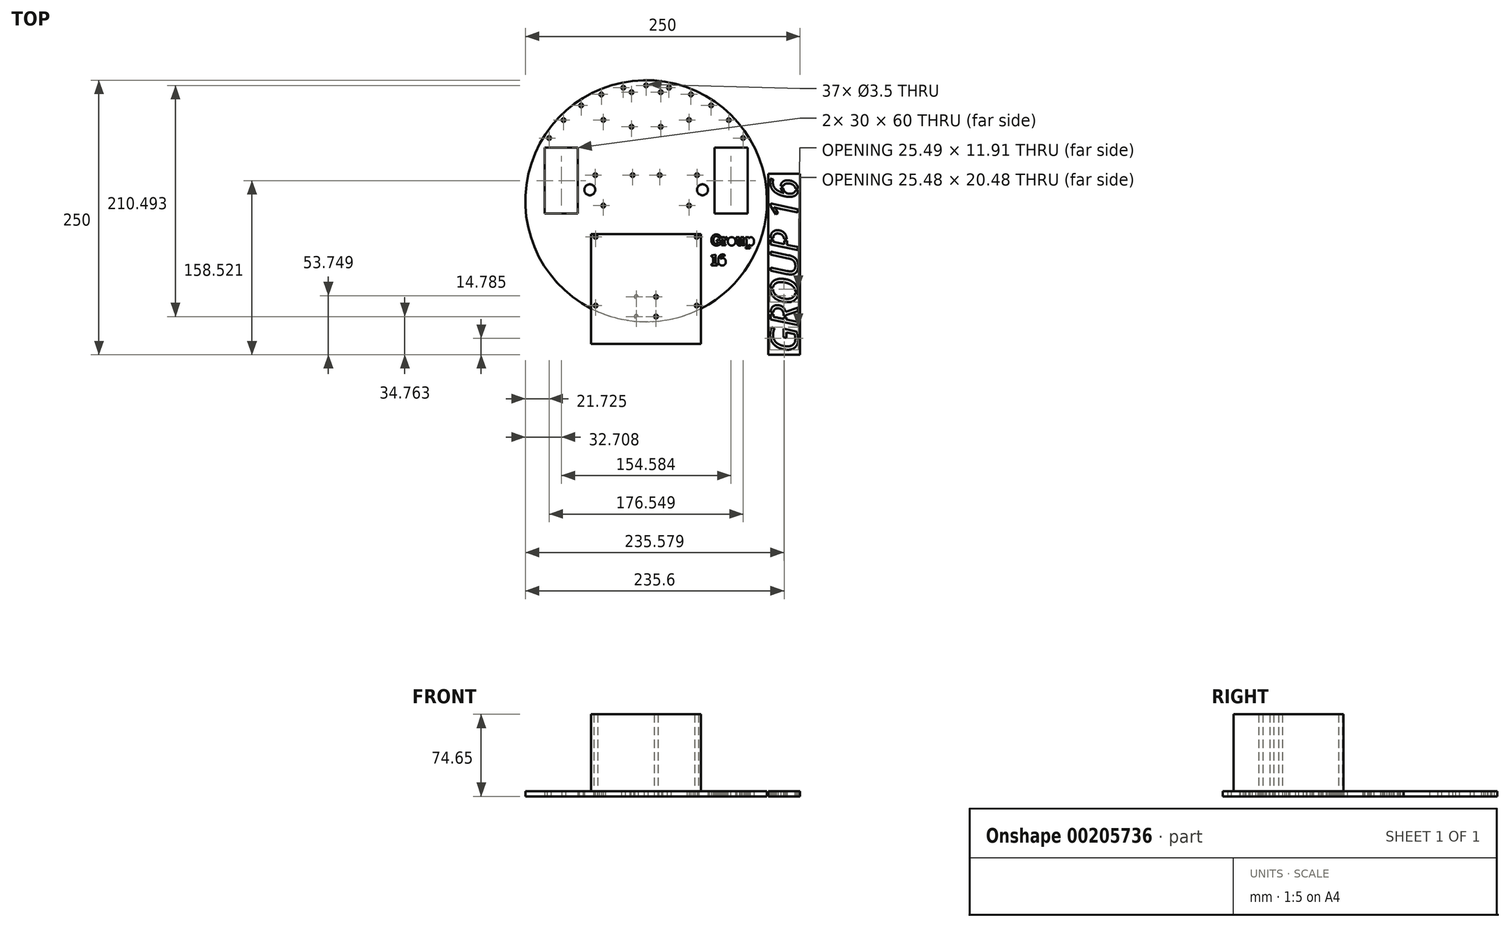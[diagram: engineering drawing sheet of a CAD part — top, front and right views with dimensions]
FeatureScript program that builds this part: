
annotation { "Feature Type Name" : "Feature", "Feature Type Description" : "" }
export const myFeature = defineFeature(function(context is Context, id is Id, definition is map)
    precondition{}
    {
        {
            var Q0;
            Q0=qCreatedBy(makeId("Top.planeOp"),FACE);
            var sketch = newSketch(context, id + "F0", { "sketchPlane" : qUnion([Q0])});
            skCircle(sketch, "E0", {"center": v(0, 0) * mm, "radius": 110 * mm});
            skLineSegment(sketch, "E1", {"start": v(0, 110) * mm, "end": v(0, 0) * mm, "construction": true});
            skCircle(sketch, "E2", {"center": v(0, 105.26) * mm, "radius": 1.75 * mm});
            skLineSegment(sketch, "E3", {"start": v(-1.75, 105.26) * mm, "end": v(1.75, 105.26) * mm, "construction": true});
            skCircle(sketch, "E4", {"center": v(-13.25, 99.05) * mm, "radius": 1.75 * mm});
            skLineSegment(sketch, "E5", {"start": v(-15, 99.05) * mm, "end": v(-11.5, 99.05) * mm, "construction": true});
            skLineSegment(sketch, "E6", {"start": v(-13.25, 100.8) * mm, "end": v(-13.25, 97.3) * mm, "construction": true});
            skLineSegment(sketch, "E7.MirrorCS", {"start": v(15, 99.05) * mm, "end": v(11.5, 99.05) * mm, "construction": true});
            skLineSegment(sketch, "E8.MirrorCS", {"start": v(13.25, 100.8) * mm, "end": v(13.25, 97.3) * mm, "construction": true});
            skCircle(sketch, "E9.MirrorC", {"center": v(13.25, 99.05) * mm, "radius": 1.75 * mm});
            skLineSegment(sketch, "E10", {"start": v(-13.25, 100.8) * mm, "end": v(-13.25, 83.3) * mm, "construction": true});
            skLineSegment(sketch, "E11", {"start": v(-16.13, 83.3) * mm, "end": v(17.46, 83.3) * mm, "construction": true});
            skCircle(sketch, "E12.MirrorC", {"center": v(-13.25, 67.55) * mm, "radius": 1.75 * mm});
            skCircle(sketch, "E13.MirrorC", {"center": v(13.25, 67.55) * mm, "radius": 1.75 * mm});
            skLineSegment(sketch, "E14.bottom", {"start": v(-92.3, 48.52) * mm, "end": v(-62.3, 48.52) * mm});
            skLineSegment(sketch, "E14.top", {"start": v(-92.3, -11.48) * mm, "end": v(-62.3, -11.48) * mm});
            skLineSegment(sketch, "E14.left", {"start": v(-92.3, 48.52) * mm, "end": v(-92.3, -11.48) * mm});
            skLineSegment(sketch, "E14.right", {"start": v(-62.3, 48.52) * mm, "end": v(-62.3, -11.48) * mm});
            skLineSegment(sketch, "E15", {"start": v(-62.3, 23.52) * mm, "end": v(-5.1, 23.52) * mm, "construction": true});
            skLineSegment(sketch, "E16", {"start": v(-43.29, 18.52) * mm, "end": v(-43.29, 23.52) * mm, "construction": true});
            skPoint(sketch, "E16.startSnap0", {"position": v(-62.3, 18.52) * mm});
            skPoint(sketch, "E16.endSnap0", {"position": v(-33.7, 23.52) * mm});
            skCircle(sketch, "E17", {"center": v(-46.3, 23.52) * mm, "radius": 1.75 * mm});
            skPoint(sketch, "E18", {"position": v(-44.54, 23.52) * mm});
            skPoint(sketch, "E19", {"position": v(-48.04, 23.52) * mm});
            skCircle(sketch, "E20", {"center": v(-12.3, 23.52) * mm, "radius": 1.75 * mm});
            skPoint(sketch, "E21", {"position": v(-14.04, 23.52) * mm});
            skPoint(sketch, "E22", {"position": v(-10.54, 23.52) * mm});
            skLineSegment(sketch, "E23.MirrorCS", {"start": v(92.3, 48.52) * mm, "end": v(62.3, 48.52) * mm});
            skLineSegment(sketch, "E24.MirrorCS", {"start": v(92.3, 48.52) * mm, "end": v(92.3, -11.48) * mm});
            skLineSegment(sketch, "E25.MirrorCS", {"start": v(62.3, 48.52) * mm, "end": v(62.3, -11.48) * mm});
            skLineSegment(sketch, "E26.MirrorCS", {"start": v(92.3, -11.48) * mm, "end": v(62.3, -11.48) * mm});
            skCircle(sketch, "E27.MirrorC", {"center": v(46.3, 23.52) * mm, "radius": 1.75 * mm});
            skCircle(sketch, "E28.MirrorC", {"center": v(12.3, 23.52) * mm, "radius": 1.75 * mm});
            skLineSegment(sketch, "E29", {"start": v(0, 0) * mm, "end": v(0, -110) * mm, "construction": true});
            skCircle(sketch, "E30", {"center": v(-9, -105.24) * mm, "radius": 1.75 * mm});
            skPoint(sketch, "E31", {"position": v(-10.75, -105.24) * mm});
            skPoint(sketch, "E32", {"position": v(-7.25, -105.24) * mm});
            skCircle(sketch, "E33", {"center": v(-9, -87.24) * mm, "radius": 1.75 * mm});
            skPoint(sketch, "E34", {"position": v(-10.75, -87.24) * mm});
            skPoint(sketch, "E35", {"position": v(-7.25, -87.24) * mm});
            skLineSegment(sketch, "E36", {"start": v(-10.75, -87.24) * mm, "end": v(0, -87.24) * mm, "construction": true});
            skLineSegment(sketch, "E37", {"start": v(-10.75, -105.24) * mm, "end": v(0, -105.24) * mm, "construction": true});
            skCircle(sketch, "E38.MirrorC", {"center": v(9, -87.24) * mm, "radius": 1.75 * mm});
            skCircle(sketch, "E39.MirrorC", {"center": v(9, -105.24) * mm, "radius": 1.75 * mm});
            skCircle(sketch, "E40.1.0", {"center": v(20.8, 103.18) * mm, "radius": 1.75 * mm});
            skCircle(sketch, "E40.2.0", {"center": v(40.79, 97.03) * mm, "radius": 1.75 * mm});
            skCircle(sketch, "E40.3.0", {"center": v(59.16, 87.05) * mm, "radius": 1.75 * mm});
            skCircle(sketch, "E40.4.0", {"center": v(75.2, 73.64) * mm, "radius": 1.75 * mm});
            skCircle(sketch, "E40.5.0", {"center": v(88.27, 57.33) * mm, "radius": 1.75 * mm});
            skLineSegment(sketch, "E40.anchor1", {"start": v(0, 0) * mm, "end": v(0, 105.26) * mm, "construction": true});
            skLineSegment(sketch, "E40.anchor2", {"start": v(0, 0) * mm, "end": v(88.27, 57.33) * mm, "construction": true});
            skCircle(sketch, "E41.1.0", {"center": v(-20.8, 103.18) * mm, "radius": 1.75 * mm});
            skCircle(sketch, "E41.2.0", {"center": v(-40.79, 97.03) * mm, "radius": 1.75 * mm});
            skCircle(sketch, "E41.3.0", {"center": v(-59.16, 87.05) * mm, "radius": 1.75 * mm});
            skCircle(sketch, "E41.4.0", {"center": v(-75.2, 73.64) * mm, "radius": 1.75 * mm});
            skCircle(sketch, "E41.5.0", {"center": v(-88.27, 57.33) * mm, "radius": 1.75 * mm});
            skLineSegment(sketch, "E41.anchor2", {"start": v(0, 0) * mm, "end": v(-88.27, 57.33) * mm, "construction": true});
            skCircle(sketch, "E42", {"center": v(-51.3, 10.17) * mm, "radius": 5 * mm});
            skCircle(sketch, "E43.MirrorC", {"center": v(51.3, 10.17) * mm, "radius": 5 * mm});
            skLineSegment(sketch, "E44.bottom", {"start": v(39, 73.8) * mm, "end": v(-39, 73.8) * mm, "construction": true});
            skLineSegment(sketch, "E44.top", {"start": v(39, -4.2) * mm, "end": v(-39, -4.2) * mm, "construction": true});
            skLineSegment(sketch, "E44.left", {"start": v(39, 73.8) * mm, "end": v(39, -4.2) * mm, "construction": true});
            skLineSegment(sketch, "E44.right", {"start": v(-39, 73.8) * mm, "end": v(-39, -4.2) * mm, "construction": true});
            skPoint(sketch, "E44.middle", {"position": v(0, 34.8) * mm});
            skPoint(sketch, "E45", {"position": v(13.25, 65.8) * mm});
            skCircle(sketch, "E46", {"center": v(39, 73.8) * mm, "radius": 1.75 * mm});
            skCircle(sketch, "E47.1.0", {"center": v(-39, 73.8) * mm, "radius": 1.75 * mm});
            skCircle(sketch, "E47.2.0", {"center": v(-39, -4.2) * mm, "radius": 1.75 * mm});
            skCircle(sketch, "E47.3.0", {"center": v(39, -4.2) * mm, "radius": 1.75 * mm});
            skLineSegment(sketch, "E48.bottom", {"start": v(-110, 110) * mm, "end": v(140, 110) * mm, "construction": true});
            skLineSegment(sketch, "E48.top", {"start": v(-110, -140) * mm, "end": v(140, -140) * mm, "construction": true});
            skLineSegment(sketch, "E48.left", {"start": v(-110, 110) * mm, "end": v(-110, -140) * mm, "construction": true});
            skLineSegment(sketch, "E48.right", {"start": v(140, 110) * mm, "end": v(140, -140) * mm, "construction": true});
            skText(sketch, "E49", { "text": "Group\n16", "fontName": "RobotoSlab-Bold.ttf"});
            skLineSegment(sketch, "E50.bottom", {"start": v(-50, -130) * mm, "end": v(50, -130) * mm});
            skLineSegment(sketch, "E50.top", {"start": v(-50, -30) * mm, "end": v(50, -30) * mm});
            skLineSegment(sketch, "E50.left", {"start": v(-50, -130) * mm, "end": v(-50, -30) * mm});
            skLineSegment(sketch, "E50.right", {"start": v(50, -130) * mm, "end": v(50, -30) * mm});
            skPoint(sketch, "E50.middle", {"position": v(0, -80) * mm});
            skLineSegment(sketch, "E51", {"start": v(-50, -30) * mm, "end": v(50, -97.98) * mm, "construction": true});
            skCircle(sketch, "E52", {"center": v(-46, -32.72) * mm, "radius": 1.75 * mm});
            skPoint(sketch, "E53", {"position": v(0, -63.99) * mm});
            skLineSegment(sketch, "E54", {"start": v(-50, -63.99) * mm, "end": v(50, -63.99) * mm, "construction": true});
            skCircle(sketch, "E55.MirrorC", {"center": v(-46, -95.26) * mm, "radius": 1.75 * mm});
            skCircle(sketch, "E56.MirrorC", {"center": v(46, -32.72) * mm, "radius": 1.75 * mm});
            skCircle(sketch, "E57.MirrorC", {"center": v(46, -95.26) * mm, "radius": 1.75 * mm});
            const initialGuessF0  = {"E49": [0.059, -0.04044, 1, 0, 0.00993]};
            skSetInitialGuess(sketch, initialGuessF0);
            skSolve(sketch);
        }
        {
            var Q0;
            Q0=makeQuery(id+"F0.imprint","IMPRINT",FACE,{"disambiguationData":[TD([[makeQuery(id+"F0.imprint","IMPRINT",EDGE,{"derivedFrom":sQuery(id+"F0.wireOp",EDGE,"E30")}),-1.0]])]});
            var Q1;
            Q1=makeQuery(id+"F0.imprint","IMPRINT",FACE,{"disambiguationData":[TD([[makeQuery(id+"F0.imprint","IMPRINT",EDGE,{"derivedFrom":sQuery(id+"F0.wireOp",EDGE,"E2")}),-1.0]])]});
            var Q2;
            Q2=makeQuery(id+"F0.imprint","IMPRINT",FACE,{"disambiguationData":[TD([[makeQuery(id+"F0.imprint","IMPRINT",EDGE,{"derivedFrom":sQuery(id+"F0.wireOp",EDGE,"E30")}),-1.0]])]});
            extrude(context, id + "F1", {"entities" : qUnion([Q0, Q1, Q2]), "depth" : 4.5 * mm});
        }
        {
            var Q0;
            Q0=makeQuery(id+"F0.imprint","IMPRINT",FACE,{"disambiguationData":[TD([[makeQuery(id+"F0.imprint","IMPRINT",EDGE,{"derivedFrom":sQuery(id+"F0.wireOp",EDGE,"E33")}),-1.0]])]});
            var Q1;
            Q1=makeQuery(id+"F0.imprint","IMPRINT",FACE,{"disambiguationData":[TD([[makeQuery(id+"F0.imprint","IMPRINT",EDGE,{"derivedFrom":sQuery(id+"F0.wireOp",EDGE,"E33")}),1.0]])]});
            var Q2;
            Q2=makeQuery(id+"F0.imprint","IMPRINT",FACE,{"disambiguationData":[TD([[makeQuery(id+"F0.imprint","IMPRINT",EDGE,{"derivedFrom":sQuery(id+"F0.wireOp",EDGE,"E38.MirrorC")}),-1.0]])]});
            var Q3;
            Q3=makeQuery(id+"F0.imprint","IMPRINT",FACE,{"disambiguationData":[TD([[makeQuery(id+"F0.imprint","IMPRINT",EDGE,{"derivedFrom":sQuery(id+"F0.wireOp",EDGE,"E39.MirrorC")}),-1.0]])]});
            var Q4;
            Q4=makeQuery(id+"F0.imprint","IMPRINT",FACE,{"disambiguationData":[TD([[makeQuery(id+"F0.imprint","IMPRINT",EDGE,{"derivedFrom":sQuery(id+"F0.wireOp",EDGE,"E30")}),1.0]])]});
            var Q5;
            {var subQ5=sQuery(id+"F0.wireOp",EDGE,"E50.bottom");Q5=makeQuery(id+"F0.imprint","IMPRINT",FACE,{"disambiguationData":[TD([[makeQuery(id+"F0.imprint","IMPRINT",EDGE,{"derivedFrom":subQ5}),1.0]])]});}
            var Q6;
            Q6=makeQuery(id+"F1.opExtrude","CAP_FACE",FACE,{"disambiguationData":[OSD([sQuery(id+"F0.wireOp",EDGE,"E0"),sQuery(id+"F0.wireOp",EDGE,"E2"),sQuery(id+"F0.wireOp",EDGE,"E4"),sQuery(id+"F0.wireOp",EDGE,"E9.MirrorC"),sQuery(id+"F0.wireOp",EDGE,"E12.MirrorC"),sQuery(id+"F0.wireOp",EDGE,"E13.MirrorC"),sQuery(id+"F0.wireOp",EDGE,"E14.bottom"),sQuery(id+"F0.wireOp",EDGE,"E14.top"),sQuery(id+"F0.wireOp",EDGE,"E14.left"),sQuery(id+"F0.wireOp",EDGE,"E14.right"),sQuery(id+"F0.wireOp",EDGE,"E17"),sQuery(id+"F0.wireOp",EDGE,"E20"),sQuery(id+"F0.wireOp",EDGE,"E23.MirrorCS"),sQuery(id+"F0.wireOp",EDGE,"E24.MirrorCS"),sQuery(id+"F0.wireOp",EDGE,"E25.MirrorCS"),sQuery(id+"F0.wireOp",EDGE,"E26.MirrorCS"),sQuery(id+"F0.wireOp",EDGE,"E27.MirrorC"),sQuery(id+"F0.wireOp",EDGE,"E28.MirrorC"),sQuery(id+"F0.wireOp",EDGE,"E30"),sQuery(id+"F0.wireOp",EDGE,"E33"),sQuery(id+"F0.wireOp",EDGE,"E38.MirrorC"),sQuery(id+"F0.wireOp",EDGE,"E39.MirrorC"),sQuery(id+"F0.wireOp",EDGE,"E40.1.0"),sQuery(id+"F0.wireOp",EDGE,"E40.2.0"),sQuery(id+"F0.wireOp",EDGE,"E40.3.0"),sQuery(id+"F0.wireOp",EDGE,"E40.4.0"),sQuery(id+"F0.wireOp",EDGE,"E40.5.0"),sQuery(id+"F0.wireOp",EDGE,"E41.1.0"),sQuery(id+"F0.wireOp",EDGE,"E41.2.0"),sQuery(id+"F0.wireOp",EDGE,"E41.3.0"),sQuery(id+"F0.wireOp",EDGE,"E41.4.0"),sQuery(id+"F0.wireOp",EDGE,"E41.5.0"),sQuery(id+"F0.wireOp",EDGE,"E42"),sQuery(id+"F0.wireOp",EDGE,"E43.MirrorC"),sQuery(id+"F0.wireOp",EDGE,"E46"),sQuery(id+"F0.wireOp",EDGE,"E47.1.0"),sQuery(id+"F0.wireOp",EDGE,"E47.2.0"),sQuery(id+"F0.wireOp",EDGE,"E47.3.0"),sQuery(id+"F0.wireOp",EDGE,"E49.sketch_text.stroke-0"),sQuery(id+"F0.wireOp",EDGE,"E49.sketch_text.stroke-1"),sQuery(id+"F0.wireOp",EDGE,"E49.sketch_text.stroke-2"),sQuery(id+"F0.wireOp",EDGE,"E49.sketch_text.stroke-3"),sQuery(id+"F0.wireOp",EDGE,"E49.sketch_text.stroke-4"),sQuery(id+"F0.wireOp",EDGE,"E49.sketch_text.stroke-5"),sQuery(id+"F0.wireOp",EDGE,"E49.sketch_text.stroke-6"),sQuery(id+"F0.wireOp",EDGE,"E49.sketch_text.stroke-7"),sQuery(id+"F0.wireOp",EDGE,"E49.sketch_text.stroke-8"),sQuery(id+"F0.wireOp",EDGE,"E49.sketch_text.stroke-9"),sQuery(id+"F0.wireOp",EDGE,"E49.sketch_text.stroke-10"),sQuery(id+"F0.wireOp",EDGE,"E49.sketch_text.stroke-11"),sQuery(id+"F0.wireOp",EDGE,"E49.sketch_text.stroke-12"),sQuery(id+"F0.wireOp",EDGE,"E49.sketch_text.stroke-13"),sQuery(id+"F0.wireOp",EDGE,"E49.sketch_text.stroke-14"),sQuery(id+"F0.wireOp",EDGE,"E49.sketch_text.stroke-15"),sQuery(id+"F0.wireOp",EDGE,"E49.sketch_text.stroke-16"),sQuery(id+"F0.wireOp",EDGE,"E49.sketch_text.stroke-17"),sQuery(id+"F0.wireOp",EDGE,"E49.sketch_text.stroke-18"),sQuery(id+"F0.wireOp",EDGE,"E49.sketch_text.stroke-19"),sQuery(id+"F0.wireOp",EDGE,"E49.sketch_text.stroke-20"),sQuery(id+"F0.wireOp",EDGE,"E49.sketch_text.stroke-21"),sQuery(id+"F0.wireOp",EDGE,"E49.sketch_text.stroke-22"),sQuery(id+"F0.wireOp",EDGE,"E49.sketch_text.stroke-23"),sQuery(id+"F0.wireOp",EDGE,"E49.sketch_text.stroke-24"),sQuery(id+"F0.wireOp",EDGE,"E49.sketch_text.stroke-25"),sQuery(id+"F0.wireOp",EDGE,"E49.sketch_text.stroke-26"),sQuery(id+"F0.wireOp",EDGE,"E49.sketch_text.stroke-27"),sQuery(id+"F0.wireOp",EDGE,"E49.sketch_text.stroke-28"),sQuery(id+"F0.wireOp",EDGE,"E49.sketch_text.stroke-29"),sQuery(id+"F0.wireOp",EDGE,"E49.sketch_text.stroke-30"),sQuery(id+"F0.wireOp",EDGE,"E49.sketch_text.stroke-31"),sQuery(id+"F0.wireOp",EDGE,"E49.sketch_text.stroke-32"),sQuery(id+"F0.wireOp",EDGE,"E49.sketch_text.stroke-33"),sQuery(id+"F0.wireOp",EDGE,"E49.sketch_text.stroke-34"),sQuery(id+"F0.wireOp",EDGE,"E49.sketch_text.stroke-35"),sQuery(id+"F0.wireOp",EDGE,"E49.sketch_text.stroke-36"),sQuery(id+"F0.wireOp",EDGE,"E49.sketch_text.stroke-37"),sQuery(id+"F0.wireOp",EDGE,"E49.sketch_text.stroke-38"),sQuery(id+"F0.wireOp",EDGE,"E49.sketch_text.stroke-39"),sQuery(id+"F0.wireOp",EDGE,"E49.sketch_text.stroke-40"),sQuery(id+"F0.wireOp",EDGE,"E49.sketch_text.stroke-41"),sQuery(id+"F0.wireOp",EDGE,"E49.sketch_text.stroke-42"),sQuery(id+"F0.wireOp",EDGE,"E49.sketch_text.stroke-43"),sQuery(id+"F0.wireOp",EDGE,"E49.sketch_text.stroke-44"),sQuery(id+"F0.wireOp",EDGE,"E49.sketch_text.stroke-45"),sQuery(id+"F0.wireOp",EDGE,"E49.sketch_text.stroke-46"),sQuery(id+"F0.wireOp",EDGE,"E49.sketch_text.stroke-47"),sQuery(id+"F0.wireOp",EDGE,"E49.sketch_text.stroke-48"),sQuery(id+"F0.wireOp",EDGE,"E49.sketch_text.stroke-49"),sQuery(id+"F0.wireOp",EDGE,"E49.sketch_text.stroke-50"),sQuery(id+"F0.wireOp",EDGE,"E49.sketch_text.stroke-51"),sQuery(id+"F0.wireOp",EDGE,"E49.sketch_text.stroke-52"),sQuery(id+"F0.wireOp",EDGE,"E49.sketch_text.stroke-53"),sQuery(id+"F0.wireOp",EDGE,"E49.sketch_text.stroke-54"),sQuery(id+"F0.wireOp",EDGE,"E49.sketch_text.stroke-65"),sQuery(id+"F0.wireOp",EDGE,"E49.sketch_text.stroke-66"),sQuery(id+"F0.wireOp",EDGE,"E49.sketch_text.stroke-67"),sQuery(id+"F0.wireOp",EDGE,"E49.sketch_text.stroke-68"),sQuery(id+"F0.wireOp",EDGE,"E49.sketch_text.stroke-69"),sQuery(id+"F0.wireOp",EDGE,"E49.sketch_text.stroke-70"),sQuery(id+"F0.wireOp",EDGE,"E49.sketch_text.stroke-71"),sQuery(id+"F0.wireOp",EDGE,"E49.sketch_text.stroke-72"),sQuery(id+"F0.wireOp",EDGE,"E49.sketch_text.stroke-73"),sQuery(id+"F0.wireOp",EDGE,"E49.sketch_text.stroke-74"),sQuery(id+"F0.wireOp",EDGE,"E49.sketch_text.stroke-75"),sQuery(id+"F0.wireOp",EDGE,"E49.sketch_text.stroke-76"),sQuery(id+"F0.wireOp",EDGE,"E49.sketch_text.stroke-77"),sQuery(id+"F0.wireOp",EDGE,"E49.sketch_text.stroke-78"),sQuery(id+"F0.wireOp",EDGE,"E49.sketch_text.stroke-79"),sQuery(id+"F0.wireOp",EDGE,"E49.sketch_text.stroke-80"),sQuery(id+"F0.wireOp",EDGE,"E49.sketch_text.stroke-81"),sQuery(id+"F0.wireOp",EDGE,"E49.sketch_text.stroke-82"),sQuery(id+"F0.wireOp",EDGE,"E49.sketch_text.stroke-83"),sQuery(id+"F0.wireOp",EDGE,"E49.sketch_text.stroke-84"),sQuery(id+"F0.wireOp",EDGE,"E49.sketch_text.stroke-85"),sQuery(id+"F0.wireOp",EDGE,"E49.sketch_text.stroke-86"),sQuery(id+"F0.wireOp",EDGE,"E49.sketch_text.stroke-87"),sQuery(id+"F0.wireOp",EDGE,"E49.sketch_text.stroke-88"),sQuery(id+"F0.wireOp",EDGE,"E49.sketch_text.stroke-89"),sQuery(id+"F0.wireOp",EDGE,"E49.sketch_text.stroke-90"),sQuery(id+"F0.wireOp",EDGE,"E49.sketch_text.stroke-91"),sQuery(id+"F0.wireOp",EDGE,"E49.sketch_text.stroke-92"),sQuery(id+"F0.wireOp",EDGE,"E49.sketch_text.stroke-93"),sQuery(id+"F0.wireOp",EDGE,"E49.sketch_text.stroke-94"),sQuery(id+"F0.wireOp",EDGE,"E49.sketch_text.stroke-95"),sQuery(id+"F0.wireOp",EDGE,"E49.sketch_text.stroke-96"),sQuery(id+"F0.wireOp",EDGE,"E49.sketch_text.stroke-97"),sQuery(id+"F0.wireOp",EDGE,"E49.sketch_text.stroke-98"),sQuery(id+"F0.wireOp",EDGE,"E49.sketch_text.stroke-99"),sQuery(id+"F0.wireOp",EDGE,"E49.sketch_text.stroke-100"),sQuery(id+"F0.wireOp",EDGE,"E49.sketch_text.stroke-101"),sQuery(id+"F0.wireOp",EDGE,"E49.sketch_text.stroke-102"),sQuery(id+"F0.wireOp",EDGE,"E49.sketch_text.stroke-103"),sQuery(id+"F0.wireOp",EDGE,"E49.sketch_text.stroke-104"),sQuery(id+"F0.wireOp",EDGE,"E49.sketch_text.stroke-105"),sQuery(id+"F0.wireOp",EDGE,"E49.sketch_text.stroke-106"),sQuery(id+"F0.wireOp",EDGE,"E49.sketch_text.stroke-107"),sQuery(id+"F0.wireOp",EDGE,"E49.sketch_text.stroke-108"),sQuery(id+"F0.wireOp",EDGE,"E49.sketch_text.stroke-119"),sQuery(id+"F0.wireOp",EDGE,"E49.sketch_text.stroke-120"),sQuery(id+"F0.wireOp",EDGE,"E49.sketch_text.stroke-121"),sQuery(id+"F0.wireOp",EDGE,"E49.sketch_text.stroke-122"),sQuery(id+"F0.wireOp",EDGE,"E49.sketch_text.stroke-123"),sQuery(id+"F0.wireOp",EDGE,"E49.sketch_text.stroke-124"),sQuery(id+"F0.wireOp",EDGE,"E49.sketch_text.stroke-125"),sQuery(id+"F0.wireOp",EDGE,"E49.sketch_text.stroke-126"),sQuery(id+"F0.wireOp",EDGE,"E49.sketch_text.stroke-127"),sQuery(id+"F0.wireOp",EDGE,"E49.sketch_text.stroke-128"),sQuery(id+"F0.wireOp",EDGE,"E49.sketch_text.stroke-129"),sQuery(id+"F0.wireOp",EDGE,"E49.sketch_text.stroke-130"),sQuery(id+"F0.wireOp",EDGE,"E49.sketch_text.stroke-131"),sQuery(id+"F0.wireOp",EDGE,"E49.sketch_text.stroke-132"),sQuery(id+"F0.wireOp",EDGE,"E49.sketch_text.stroke-133"),sQuery(id+"F0.wireOp",EDGE,"E49.sketch_text.stroke-134"),sQuery(id+"F0.wireOp",EDGE,"E49.sketch_text.stroke-135"),sQuery(id+"F0.wireOp",EDGE,"E49.sketch_text.stroke-136"),sQuery(id+"F0.wireOp",EDGE,"E49.sketch_text.stroke-137"),sQuery(id+"F0.wireOp",EDGE,"E49.sketch_text.stroke-138"),sQuery(id+"F0.wireOp",EDGE,"E49.sketch_text.stroke-139"),sQuery(id+"F0.wireOp",EDGE,"E49.sketch_text.stroke-140"),sQuery(id+"F0.wireOp",EDGE,"E49.sketch_text.stroke-141"),sQuery(id+"F0.wireOp",EDGE,"E49.sketch_text.stroke-142"),sQuery(id+"F0.wireOp",EDGE,"E49.sketch_text.stroke-143"),sQuery(id+"F0.wireOp",EDGE,"E49.sketch_text.stroke-144"),sQuery(id+"F0.wireOp",EDGE,"E49.sketch_text.stroke-145"),sQuery(id+"F0.wireOp",EDGE,"E49.sketch_text.stroke-146"),sQuery(id+"F0.wireOp",EDGE,"E49.sketch_text.stroke-147"),sQuery(id+"F0.wireOp",EDGE,"E52"),sQuery(id+"F0.wireOp",EDGE,"E55.MirrorC"),sQuery(id+"F0.wireOp",EDGE,"E56.MirrorC"),sQuery(id+"F0.wireOp",EDGE,"E57.MirrorC")])],"isStart":false});
            extrude(context, id + "F2", {"entities" : qUnion([Q0, Q1, Q2, Q3, Q4, Q5]), "depth" : 74.65 * mm, "hasSecondDirection" : true, "secondDirectionBound" : SecondDirectionBoundingType.UP_TO_SURFACE, "secondDirectionOppositeDirection" : false, "secondDirectionBoundEntityFace" : qUnion([Q6]), "secondDirectionDepth" : 25 * mm});
        }
        {
            var Q0;
            Q0=qCreatedBy(makeId("Top.planeOp"),FACE);
            var sketch = newSketch(context, id + "F3", { "sketchPlane" : qUnion([Q0])});
            skText(sketch, "E58", { "text": "GROUP 16", "fontName": "OpenSans-Italic.ttf"});
            skLineSegment(sketch, "E59.bottom", {"start": v(140, -140) * mm, "end": v(111, -140) * mm});
            skLineSegment(sketch, "E59.top", {"start": v(140, 24.66) * mm, "end": v(111, 24.66) * mm});
            skLineSegment(sketch, "E59.left", {"start": v(140, -140) * mm, "end": v(140, 24.66) * mm});
            skLineSegment(sketch, "E59.right", {"start": v(111, -140) * mm, "end": v(111, 24.66) * mm});
            skLineSegment(sketch, "E60", {"start": v(135.08, -83.73) * mm, "end": v(138.7, -83.73) * mm});
            skLineSegment(sketch, "E61", {"start": v(138.7, -82.23) * mm, "end": v(135.08, -82.23) * mm});
            skLineSegment(sketch, "E62", {"start": v(112.27, -78.8) * mm, "end": v(115.89, -78.8) * mm});
            skLineSegment(sketch, "E63", {"start": v(115.89, -80.3) * mm, "end": v(112.27, -80.3) * mm});
            skLineSegment(sketch, "E64", {"start": v(114.08, -80.3) * mm, "end": v(114.08, -78.8) * mm, "construction": true});
            skLineSegment(sketch, "E65", {"start": v(136.89, -82.23) * mm, "end": v(136.89, -83.73) * mm, "construction": true});
            skLineSegment(sketch, "E66", {"start": v(124.62, -34.58) * mm, "end": v(129.02, -34.58) * mm});
            skLineSegment(sketch, "E67", {"start": v(129.02, -36.29) * mm, "end": v(124.62, -36.29) * mm});
            skLineSegment(sketch, "E68", {"start": v(126.82, -36.29) * mm, "end": v(126.82, -34.58) * mm, "construction": true});
            skLineSegment(sketch, "E69", {"start": v(112.63, -33.52) * mm, "end": v(116.74, -33.52) * mm});
            skLineSegment(sketch, "E70", {"start": v(116.74, -35.23) * mm, "end": v(112.63, -35.23) * mm});
            skLineSegment(sketch, "E71", {"start": v(114.69, -35.23) * mm, "end": v(114.69, -33.52) * mm, "construction": true});
            skLineSegment(sketch, "E72", {"start": v(121.89, 13.57) * mm, "end": v(126, 13.57) * mm});
            skLineSegment(sketch, "E73", {"start": v(126, 11.86) * mm, "end": v(121.89, 11.86) * mm});
            skLineSegment(sketch, "E74", {"start": v(123.95, 11.86) * mm, "end": v(123.95, 13.57) * mm, "construction": true});
            skLineSegment(sketch, "E75", {"start": v(134.58, 11.2) * mm, "end": v(138.7, 11.2) * mm});
            skLineSegment(sketch, "E76", {"start": v(138.7, 9.48) * mm, "end": v(134.58, 9.48) * mm});
            skLineSegment(sketch, "E77", {"start": v(136.64, 9.48) * mm, "end": v(136.64, 11.2) * mm, "construction": true});
            skLineSegment(sketch, "E78", {"start": v(112.66, -101.4) * mm, "end": v(116.78, -101.4) * mm});
            skLineSegment(sketch, "E79", {"start": v(116.78, -103.1) * mm, "end": v(112.66, -103.1) * mm});
            skLineSegment(sketch, "E80", {"start": v(114.72, -103.1) * mm, "end": v(114.72, -101.4) * mm, "construction": true});
            skLineSegment(sketch, "E81", {"start": v(124.67, -104.47) * mm, "end": v(128.78, -104.47) * mm});
            skLineSegment(sketch, "E82", {"start": v(128.78, -106.17) * mm, "end": v(124.67, -106.17) * mm});
            skLineSegment(sketch, "E83", {"start": v(126.72, -106.17) * mm, "end": v(126.72, -104.47) * mm, "construction": true});
            const initialGuessF3  = {"E58": [0.138, -0.138, 0, 1, 0.025]};
            skSetInitialGuess(sketch, initialGuessF3);
            skSolve(sketch);
        }
        {
            var Q0;
            Q0=makeQuery(id+"F3.imprint","IMPRINT",FACE,{"disambiguationData":[TD([[makeQuery(id+"F3.imprint","IMPRINT",EDGE,{"derivedFrom":sQuery(id+"F3.wireOp",EDGE,"E58.sketch_text.stroke-0")}),1.0]])]});
            var Q1;
            {var subQ9=sQuery(id+"F3.wireOp",EDGE,"E58.sketch_text.stroke-32");Q1=makeQuery(id+"F3.imprint","IMPRINT",FACE,{"disambiguationData":[TD([[makeQuery(id+"F3.imprint","IMPRINT",EDGE,{"derivedFrom":subQ9}),1.0]])]});}
            var Q2;
            {var subQ12=sQuery(id+"F3.wireOp",EDGE,"E58.sketch_text.stroke-50");Q2=makeQuery(id+"F3.imprint","IMPRINT",FACE,{"disambiguationData":[TD([[makeQuery(id+"F3.imprint","IMPRINT",EDGE,{"derivedFrom":subQ12}),1.0]])]});}
            var Q3;
            {var subQ7=sQuery(id+"F3.wireOp",EDGE,"E58.sketch_text.stroke-84");Q3=makeQuery(id+"F3.imprint","IMPRINT",FACE,{"disambiguationData":[TD([[makeQuery(id+"F3.imprint","IMPRINT",EDGE,{"derivedFrom":subQ7}),1.0]])]});}
            var Q4;
            {var subQ12=sQuery(id+"F3.wireOp",EDGE,"E58.sketch_text.stroke-120");Q4=makeQuery(id+"F3.imprint","IMPRINT",FACE,{"disambiguationData":[TD([[makeQuery(id+"F3.imprint","IMPRINT",EDGE,{"derivedFrom":subQ12}),1.0]])]});}
            var Q5;
            {var subQ0=sQuery(id+"F3.wireOp",EDGE,"E81");var subQ1=sQuery(id+"F3.wireOp",EDGE,"E58.sketch_text.stroke-31");var subQ2=makeQuery(id+"F3.imprint","INTERSECT",VERTEX,{"derivedFrom":[subQ1,subQ0]});Q5=makeQuery(id+"F3.imprint","IMPRINT",FACE,{"disambiguationData":[TD([[makeQuery(id+"F3.imprint","IMPRINT",EDGE,{"disambiguationData":[TD([[subQ2,-1.0]])],"derivedFrom":subQ1}),-1.0]])]});}
            var Q6;
            {var subQ5=sQuery(id+"F3.wireOp",EDGE,"E58.sketch_text.stroke-26");var subQ6=sQuery(id+"F3.wireOp",EDGE,"E58.sketch_text.stroke-25");var subQ7=makeQuery(id+"F3.imprint","INTERSECT",VERTEX,{"derivedFrom":[subQ6,subQ5]});Q6=makeQuery(id+"F3.imprint","IMPRINT",FACE,{"disambiguationData":[TD([[makeQuery(id+"F3.imprint","IMPRINT",EDGE,{"disambiguationData":[TD([[subQ7,1.0]])],"derivedFrom":subQ6}),-1.0]])]});}
            var Q7;
            {var subQ5=sQuery(id+"F3.wireOp",EDGE,"E58.sketch_text.stroke-47");var subQ6=sQuery(id+"F3.wireOp",EDGE,"E58.sketch_text.stroke-46");var subQ7=makeQuery(id+"F3.imprint","INTERSECT",VERTEX,{"derivedFrom":[subQ6,subQ5]});Q7=makeQuery(id+"F3.imprint","IMPRINT",FACE,{"disambiguationData":[TD([[makeQuery(id+"F3.imprint","IMPRINT",EDGE,{"disambiguationData":[TD([[subQ7,1.0]])],"derivedFrom":subQ6}),-1.0]])]});}
            var Q8;
            {var subQ7=sQuery(id+"F3.wireOp",EDGE,"E58.sketch_text.stroke-42");var subQ8=sQuery(id+"F3.wireOp",EDGE,"E58.sketch_text.stroke-41");var subQ9=makeQuery(id+"F3.imprint","INTERSECT",VERTEX,{"derivedFrom":[subQ8,subQ7]});Q8=makeQuery(id+"F3.imprint","IMPRINT",FACE,{"disambiguationData":[TD([[makeQuery(id+"F3.imprint","IMPRINT",EDGE,{"disambiguationData":[TD([[subQ9,1.0]])],"derivedFrom":subQ8}),-1.0]])]});}
            var Q9;
            {var subQ0=sQuery(id+"F3.wireOp",EDGE,"E66");var subQ1=sQuery(id+"F3.wireOp",EDGE,"E58.sketch_text.stroke-76");var subQ2=makeQuery(id+"F3.imprint","INTERSECT",VERTEX,{"derivedFrom":[subQ1,subQ0]});Q9=makeQuery(id+"F3.imprint","IMPRINT",FACE,{"disambiguationData":[TD([[makeQuery(id+"F3.imprint","IMPRINT",EDGE,{"disambiguationData":[TD([[subQ2,-1.0]])],"derivedFrom":subQ1}),-1.0]])]});}
            var Q10;
            {var subQ7=sQuery(id+"F3.wireOp",EDGE,"E58.sketch_text.stroke-82");var subQ8=sQuery(id+"F3.wireOp",EDGE,"E58.sketch_text.stroke-81");var subQ9=makeQuery(id+"F3.imprint","INTERSECT",VERTEX,{"derivedFrom":[subQ8,subQ7]});Q10=makeQuery(id+"F3.imprint","IMPRINT",FACE,{"disambiguationData":[TD([[makeQuery(id+"F3.imprint","IMPRINT",EDGE,{"disambiguationData":[TD([[subQ9,1.0]])],"derivedFrom":subQ8}),-1.0]])]});}
            var Q11;
            {var subQ6=sQuery(id+"F3.wireOp",EDGE,"E58.sketch_text.stroke-112");var subQ9=sQuery(id+"F3.wireOp",EDGE,"E58.sketch_text.stroke-111");var subQ10=makeQuery(id+"F3.imprint","INTERSECT",VERTEX,{"derivedFrom":[subQ9,subQ6]});Q11=makeQuery(id+"F3.imprint","IMPRINT",FACE,{"disambiguationData":[TD([[makeQuery(id+"F3.imprint","IMPRINT",EDGE,{"disambiguationData":[TD([[subQ10,1.0]])],"derivedFrom":subQ9}),-1.0]])]});}
            var Q12;
            {var subQ7=sQuery(id+"F3.wireOp",EDGE,"E58.sketch_text.stroke-117");var subQ8=sQuery(id+"F3.wireOp",EDGE,"E58.sketch_text.stroke-116");var subQ9=makeQuery(id+"F3.imprint","INTERSECT",VERTEX,{"derivedFrom":[subQ8,subQ7]});Q12=makeQuery(id+"F3.imprint","IMPRINT",FACE,{"disambiguationData":[TD([[makeQuery(id+"F3.imprint","IMPRINT",EDGE,{"disambiguationData":[TD([[subQ9,1.0]])],"derivedFrom":subQ8}),-1.0]])]});}
            extrude(context, id + "F4", {"entities" : qUnion([Q0, Q1, Q2, Q3, Q4, Q5, Q6, Q7, Q8, Q9, Q10, Q11, Q12]), "depth" : 4.5 * mm});
        }
    });
